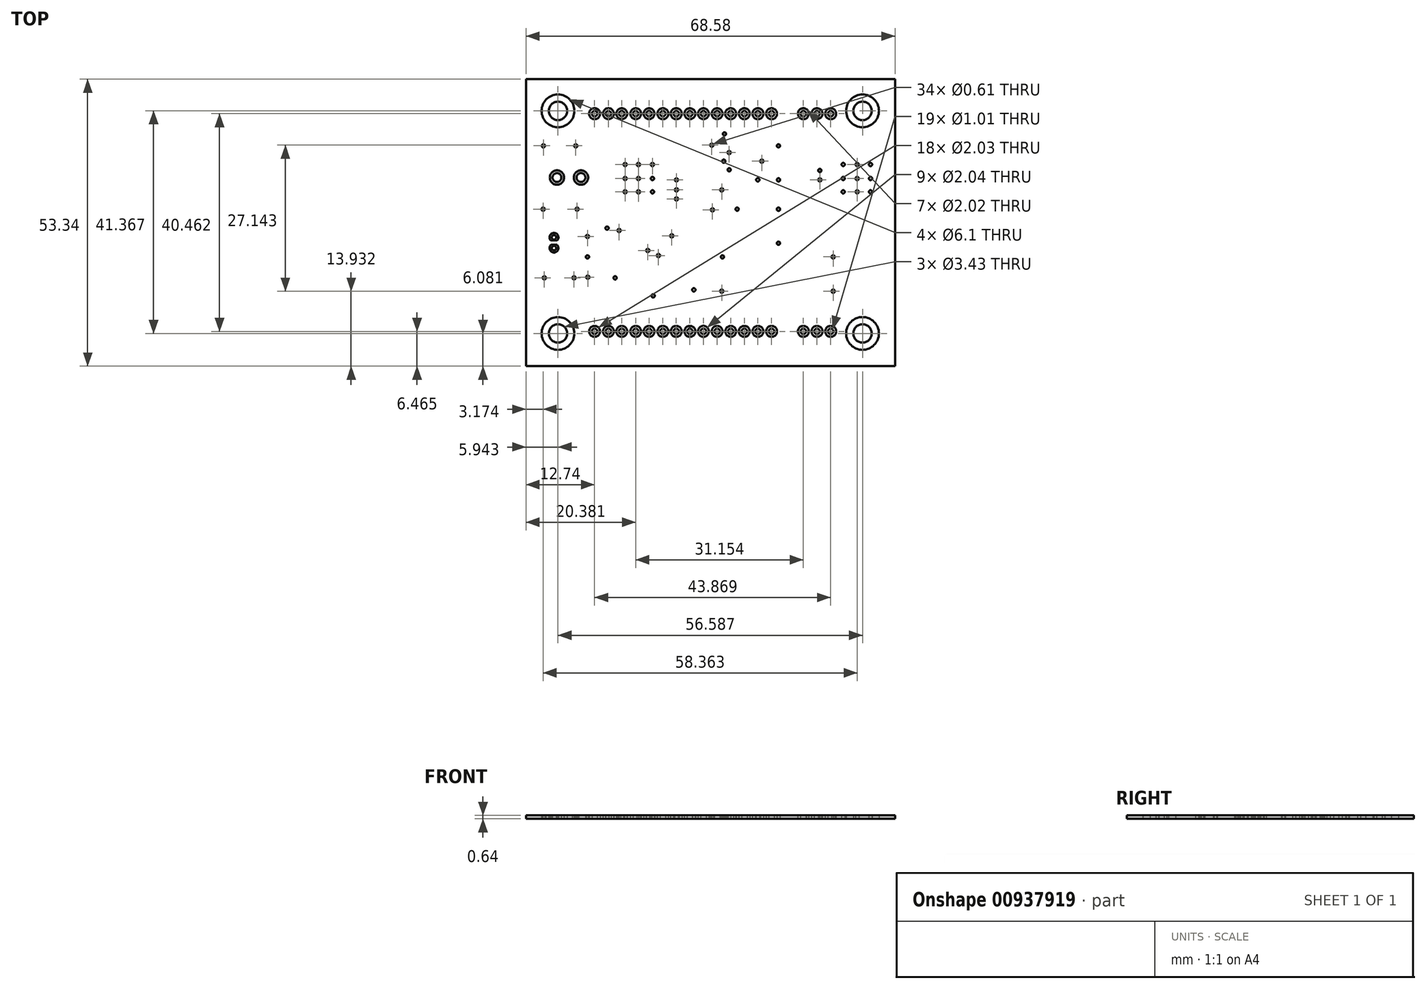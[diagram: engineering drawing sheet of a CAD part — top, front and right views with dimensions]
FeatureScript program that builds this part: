
annotation { "Feature Type Name" : "Feature", "Feature Type Description" : "" }
export const myFeature = defineFeature(function(context is Context, id is Id, definition is map)
    precondition{}
    {
        {
            var Q0;
            Q0=qCreatedBy(makeId("Top.planeOp"),FACE);
            var sketch = newSketch(context, id + "F0", { "sketchPlane" : qUnion([Q0])});
            skLineSegment(sketch, "E0.bottom", {"start": v(-43.28, 27.62) * mm, "end": v(25.3, 27.62) * mm});
            skLineSegment(sketch, "E0.top", {"start": v(-43.28, -25.72) * mm, "end": v(25.3, -25.72) * mm});
            skLineSegment(sketch, "E0.left", {"start": v(-43.28, 27.62) * mm, "end": v(-43.28, -25.72) * mm});
            skLineSegment(sketch, "E0.right", {"start": v(25.3, 27.62) * mm, "end": v(25.3, -25.72) * mm});
            skCircle(sketch, "E1", {"center": v(-37.34, -19.64) * mm, "radius": 1.71 * mm});
            skCircle(sketch, "E2", {"center": v(-37.34, -19.64) * mm, "radius": 3.05 * mm});
            skCircle(sketch, "E3", {"center": v(19.25, -19.64) * mm, "radius": 1.71 * mm});
            skCircle(sketch, "E4", {"center": v(19.25, -19.64) * mm, "radius": 3.05 * mm});
            skCircle(sketch, "E5", {"center": v(19.25, 21.73) * mm, "radius": 1.71 * mm});
            skCircle(sketch, "E6", {"center": v(19.25, 21.73) * mm, "radius": 3.05 * mm});
            skCircle(sketch, "E7", {"center": v(-37.34, 21.73) * mm, "radius": 1.71 * mm});
            skCircle(sketch, "E8", {"center": v(-37.34, 21.73) * mm, "radius": 3.05 * mm});
            skCircle(sketch, "E9", {"center": v(-38.09, -3.77) * mm, "radius": 0.4 * mm});
            skCircle(sketch, "E10", {"center": v(-38.09, -1.79) * mm, "radius": 0.4 * mm});
            skArc(sketch, "E11", {"start": v(-38.7, -2.35) * mm, "mid": v(-38.08, -0.95) * mm, "end": v(-37.48, -2.35) * mm});
            skLineSegment(sketch, "E12", {"start": v(-38.7, -2.35) * mm, "end": v(-37.48, -2.35) * mm});
            skArc(sketch, "E13", {"start": v(-37.51, -3.19) * mm, "mid": v(-38.09, -4.6) * mm, "end": v(-38.66, -3.19) * mm});
            skLineSegment(sketch, "E14", {"start": v(-38.66, -3.19) * mm, "end": v(-37.51, -3.19) * mm});
            skCircle(sketch, "E15", {"center": v(-37.53, 9.34) * mm, "radius": 0.82 * mm});
            skCircle(sketch, "E16", {"center": v(-37.53, 9.34) * mm, "radius": 1.33 * mm});
            skCircle(sketch, "E17", {"center": v(-33.07, 9.34) * mm, "radius": 0.83 * mm});
            skCircle(sketch, "E18", {"center": v(-33.07, 9.34) * mm, "radius": 1.33 * mm});
            skCircle(sketch, "E19", {"center": v(-30.54, -19.26) * mm, "radius": 0.5 * mm});
            skCircle(sketch, "E20", {"center": v(-30.54, -19.26) * mm, "radius": 1.02 * mm});
            skCircle(sketch, "E21", {"center": v(-27.96, -19.26) * mm, "radius": 0.5 * mm});
            skCircle(sketch, "E22", {"center": v(-25.49, -19.26) * mm, "radius": 0.5 * mm});
            skCircle(sketch, "E23", {"center": v(-22.9, -19.26) * mm, "radius": 0.5 * mm});
            skCircle(sketch, "E24", {"center": v(-20.42, -19.26) * mm, "radius": 0.5 * mm});
            skCircle(sketch, "E25", {"center": v(-17.85, -19.26) * mm, "radius": 0.5 * mm});
            skCircle(sketch, "E26", {"center": v(-15.36, -19.26) * mm, "radius": 0.5 * mm});
            skCircle(sketch, "E27", {"center": v(-12.83, -19.26) * mm, "radius": 0.51 * mm});
            skCircle(sketch, "E28", {"center": v(-10.31, -19.26) * mm, "radius": 0.5 * mm});
            skCircle(sketch, "E29", {"center": v(-7.76, -19.26) * mm, "radius": 0.5 * mm});
            skCircle(sketch, "E30", {"center": v(-5.25, -19.26) * mm, "radius": 0.5 * mm});
            skCircle(sketch, "E31", {"center": v(-2.71, -19.26) * mm, "radius": 0.5 * mm});
            skCircle(sketch, "E32", {"center": v(-0.19, -19.26) * mm, "radius": 0.5 * mm});
            skCircle(sketch, "E33", {"center": v(2.35, -19.26) * mm, "radius": 0.5 * mm});
            skCircle(sketch, "E34", {"center": v(-27.96, 21.2) * mm, "radius": 0.5 * mm});
            skCircle(sketch, "E35", {"center": v(-30.54, 21.2) * mm, "radius": 0.5 * mm});
            skCircle(sketch, "E36", {"center": v(-25.49, 21.2) * mm, "radius": 0.5 * mm});
            skCircle(sketch, "E37", {"center": v(-22.9, 21.2) * mm, "radius": 0.5 * mm});
            skCircle(sketch, "E38", {"center": v(-20.42, 21.2) * mm, "radius": 0.51 * mm});
            skCircle(sketch, "E39", {"center": v(-17.85, 21.2) * mm, "radius": 0.5 * mm});
            skCircle(sketch, "E40", {"center": v(-15.36, 21.2) * mm, "radius": 0.51 * mm});
            skCircle(sketch, "E41", {"center": v(-12.83, 21.2) * mm, "radius": 0.5 * mm});
            skCircle(sketch, "E42", {"center": v(-7.76, 21.2) * mm, "radius": 0.51 * mm});
            skCircle(sketch, "E43", {"center": v(-10.31, 21.2) * mm, "radius": 0.5 * mm});
            skCircle(sketch, "E44", {"center": v(-5.25, 21.2) * mm, "radius": 0.5 * mm});
            skCircle(sketch, "E45", {"center": v(-2.71, 21.2) * mm, "radius": 0.5 * mm});
            skCircle(sketch, "E46", {"center": v(-0.19, 21.2) * mm, "radius": 0.5 * mm});
            skCircle(sketch, "E47", {"center": v(2.35, 21.2) * mm, "radius": 0.5 * mm});
            skCircle(sketch, "E48", {"center": v(8.25, -19.26) * mm, "radius": 0.5 * mm});
            skCircle(sketch, "E49", {"center": v(10.79, -19.26) * mm, "radius": 0.5 * mm});
            skCircle(sketch, "E50", {"center": v(13.33, -19.26) * mm, "radius": 0.5 * mm});
            skCircle(sketch, "E51", {"center": v(8.25, 21.2) * mm, "radius": 0.51 * mm});
            skCircle(sketch, "E52", {"center": v(10.79, 21.2) * mm, "radius": 0.5 * mm});
            skCircle(sketch, "E53", {"center": v(13.33, 21.2) * mm, "radius": 0.51 * mm});
            skCircle(sketch, "E54", {"center": v(13.33, 21.2) * mm, "radius": 1.02 * mm});
            skCircle(sketch, "E55", {"center": v(10.79, 21.2) * mm, "radius": 1.02 * mm});
            skCircle(sketch, "E56", {"center": v(8.25, 21.2) * mm, "radius": 1.01 * mm});
            skCircle(sketch, "E57", {"center": v(2.35, 21.2) * mm, "radius": 1.02 * mm});
            skCircle(sketch, "E58", {"center": v(-0.19, 21.2) * mm, "radius": 1.02 * mm});
            skCircle(sketch, "E59", {"center": v(-2.71, 21.2) * mm, "radius": 1.01 * mm});
            skCircle(sketch, "E60", {"center": v(-5.25, 21.2) * mm, "radius": 1.02 * mm});
            skCircle(sketch, "E61", {"center": v(-7.76, 21.2) * mm, "radius": 1.01 * mm});
            skCircle(sketch, "E62", {"center": v(-10.31, 21.2) * mm, "radius": 1.01 * mm});
            skCircle(sketch, "E63", {"center": v(-12.83, 21.2) * mm, "radius": 1.01 * mm});
            skCircle(sketch, "E64", {"center": v(-15.36, 21.2) * mm, "radius": 1.02 * mm});
            skCircle(sketch, "E65", {"center": v(-17.85, 21.2) * mm, "radius": 1.02 * mm});
            skCircle(sketch, "E66", {"center": v(-20.42, 21.2) * mm, "radius": 1.01 * mm});
            skCircle(sketch, "E67", {"center": v(-22.9, 21.2) * mm, "radius": 1.01 * mm});
            skCircle(sketch, "E68", {"center": v(-25.49, 21.2) * mm, "radius": 1.01 * mm});
            skCircle(sketch, "E69", {"center": v(-27.96, 21.2) * mm, "radius": 1.02 * mm});
            skCircle(sketch, "E70", {"center": v(-30.54, 21.2) * mm, "radius": 1.02 * mm});
            skCircle(sketch, "E71", {"center": v(13.33, -19.26) * mm, "radius": 1.01 * mm});
            skCircle(sketch, "E72", {"center": v(10.79, -19.26) * mm, "radius": 1.02 * mm});
            skCircle(sketch, "E73", {"center": v(8.25, -19.26) * mm, "radius": 1.02 * mm});
            skCircle(sketch, "E74", {"center": v(2.35, -19.26) * mm, "radius": 1.02 * mm});
            skCircle(sketch, "E75", {"center": v(-0.19, -19.26) * mm, "radius": 1.02 * mm});
            skCircle(sketch, "E76", {"center": v(-2.71, -19.26) * mm, "radius": 1.01 * mm});
            skCircle(sketch, "E77", {"center": v(-5.25, -19.26) * mm, "radius": 1 * mm});
            skCircle(sketch, "E78", {"center": v(-7.76, -19.26) * mm, "radius": 1.01 * mm});
            skCircle(sketch, "E79", {"center": v(-10.31, -19.26) * mm, "radius": 1.02 * mm});
            skCircle(sketch, "E80", {"center": v(-12.83, -19.26) * mm, "radius": 1.02 * mm});
            skCircle(sketch, "E81", {"center": v(-15.36, -19.26) * mm, "radius": 1.02 * mm});
            skCircle(sketch, "E82", {"center": v(-17.85, -19.26) * mm, "radius": 1.01 * mm});
            skCircle(sketch, "E83", {"center": v(-20.42, -19.26) * mm, "radius": 1.01 * mm});
            skCircle(sketch, "E84", {"center": v(-22.9, -19.26) * mm, "radius": 1.01 * mm});
            skCircle(sketch, "E85", {"center": v(-25.49, -19.26) * mm, "radius": 1.01 * mm});
            skCircle(sketch, "E86", {"center": v(-27.96, -19.26) * mm, "radius": 1.02 * mm});
            skCircle(sketch, "E87", {"center": v(-39.87, -9.3) * mm, "radius": 0.3 * mm});
            skCircle(sketch, "E88", {"center": v(-34.36, -9.3) * mm, "radius": 0.3 * mm});
            skCircle(sketch, "E89", {"center": v(-31.8, -9.18) * mm, "radius": 0.3 * mm});
            skCircle(sketch, "E90", {"center": v(-26.73, -9.3) * mm, "radius": 0.3 * mm});
            skCircle(sketch, "E91", {"center": v(-31.86, -5.4) * mm, "radius": 0.31 * mm});
            skCircle(sketch, "E92", {"center": v(-31.86, -1.62) * mm, "radius": 0.3 * mm});
            skCircle(sketch, "E93", {"center": v(-28.21, -0.07) * mm, "radius": 0.3 * mm});
            skCircle(sketch, "E94", {"center": v(-33.79, 3.46) * mm, "radius": 0.3 * mm});
            skCircle(sketch, "E95", {"center": v(-40.1, 3.46) * mm, "radius": 0.3 * mm});
            skCircle(sketch, "E96", {"center": v(-40.05, 15.23) * mm, "radius": 0.3 * mm});
            skCircle(sketch, "E97", {"center": v(-34.03, 15.23) * mm, "radius": 0.3 * mm});
            skCircle(sketch, "E98", {"center": v(-24.86, 11.76) * mm, "radius": 0.3 * mm});
            skCircle(sketch, "E99", {"center": v(-22.4, 11.76) * mm, "radius": 0.3 * mm});
            skCircle(sketch, "E100", {"center": v(-22.39, 9.16) * mm, "radius": 0.3 * mm});
            skCircle(sketch, "E101", {"center": v(-24.86, 9.16) * mm, "radius": 0.3 * mm});
            skCircle(sketch, "E102", {"center": v(-19.79, 11.76) * mm, "radius": 0.3 * mm});
            skCircle(sketch, "E103", {"center": v(-19.79, 9.16) * mm, "radius": 0.3 * mm});
            skCircle(sketch, "E104", {"center": v(-19.78, 6.68) * mm, "radius": 0.3 * mm});
            skCircle(sketch, "E105", {"center": v(-22.39, 6.68) * mm, "radius": 0.3 * mm});
            skCircle(sketch, "E106", {"center": v(-24.86, 6.69) * mm, "radius": 0.3 * mm});
            skCircle(sketch, "E107", {"center": v(-15.33, 8.9) * mm, "radius": 0.3 * mm});
            skCircle(sketch, "E108", {"center": v(-15.32, 7.05) * mm, "radius": 0.3 * mm});
            skCircle(sketch, "E109", {"center": v(-15.32, 5.37) * mm, "radius": 0.3 * mm});
            skCircle(sketch, "E110", {"center": v(-25.98, -0.5) * mm, "radius": 0.3 * mm});
            skCircle(sketch, "E111", {"center": v(-20.65, -4.22) * mm, "radius": 0.3 * mm});
            skCircle(sketch, "E112", {"center": v(-18.67, -5.16) * mm, "radius": 0.3 * mm});
            skCircle(sketch, "E113", {"center": v(-16.2, -1.5) * mm, "radius": 0.3 * mm});
            skCircle(sketch, "E114", {"center": v(-6.78, -5.4) * mm, "radius": 0.3 * mm});
            skCircle(sketch, "E115", {"center": v(-19.66, -12.65) * mm, "radius": 0.3 * mm});
            skCircle(sketch, "E116", {"center": v(-12.1, -11.54) * mm, "radius": 0.3 * mm});
            skCircle(sketch, "E117", {"center": v(-6.9, -11.78) * mm, "radius": 0.3 * mm});
            skCircle(sketch, "E118", {"center": v(3.64, -2.86) * mm, "radius": 0.3 * mm});
            skCircle(sketch, "E119", {"center": v(13.8, -11.79) * mm, "radius": 0.3 * mm});
            skCircle(sketch, "E120", {"center": v(13.8, -5.4) * mm, "radius": 0.3 * mm});
            skCircle(sketch, "E121", {"center": v(-8.63, 3.33) * mm, "radius": 0.3 * mm});
            skCircle(sketch, "E122", {"center": v(-6.9, 7.05) * mm, "radius": 0.3 * mm});
            skCircle(sketch, "E123", {"center": v(-4.05, 3.46) * mm, "radius": 0.3 * mm});
            skCircle(sketch, "E124", {"center": v(3.63, 3.46) * mm, "radius": 0.31 * mm});
            skCircle(sketch, "E125", {"center": v(-0.2, 8.91) * mm, "radius": 0.3 * mm});
            skCircle(sketch, "E126", {"center": v(0.54, 12.38) * mm, "radius": 0.3 * mm});
            skCircle(sketch, "E127", {"center": v(-5.53, 10.78) * mm, "radius": 0.3 * mm});
            skCircle(sketch, "E128", {"center": v(-6.53, 12.38) * mm, "radius": 0.3 * mm});
            skCircle(sketch, "E129", {"center": v(-5.53, 13.98) * mm, "radius": 0.3 * mm});
            skCircle(sketch, "E130", {"center": v(-8.76, 15.36) * mm, "radius": 0.3 * mm});
            skCircle(sketch, "E131", {"center": v(-6.4, 17.46) * mm, "radius": 0.3 * mm});
            skCircle(sketch, "E132", {"center": v(3.63, 8.9) * mm, "radius": 0.3 * mm});
            skCircle(sketch, "E133", {"center": v(3.63, 15.24) * mm, "radius": 0.3 * mm});
            skCircle(sketch, "E134", {"center": v(11.32, 8.9) * mm, "radius": 0.3 * mm});
            skCircle(sketch, "E135", {"center": v(11.32, 10.64) * mm, "radius": 0.3 * mm});
            skCircle(sketch, "E136", {"center": v(15.65, 6.68) * mm, "radius": 0.3 * mm});
            skCircle(sketch, "E137", {"center": v(15.65, 9.16) * mm, "radius": 0.3 * mm});
            skCircle(sketch, "E138", {"center": v(15.66, 11.76) * mm, "radius": 0.3 * mm});
            skCircle(sketch, "E139", {"center": v(18.25, 11.76) * mm, "radius": 0.3 * mm});
            skCircle(sketch, "E140", {"center": v(18.25, 9.15) * mm, "radius": 0.3 * mm});
            skCircle(sketch, "E141", {"center": v(18.26, 6.68) * mm, "radius": 0.3 * mm});
            skCircle(sketch, "E142", {"center": v(20.73, 6.68) * mm, "radius": 0.3 * mm});
            skCircle(sketch, "E143", {"center": v(20.73, 9.16) * mm, "radius": 0.3 * mm});
            skCircle(sketch, "E144", {"center": v(20.73, 11.76) * mm, "radius": 0.3 * mm});
            skSolve(sketch);
        }
        {
            var Q0;
            Q0=makeQuery(id+"F0.imprint","IMPRINT",FACE,{"disambiguationData":[TD([[makeQuery(id+"F0.imprint","IMPRINT",EDGE,{"derivedFrom":sQuery(id+"F0.wireOp",EDGE,"E102")}),1.0]])]});
            var Q1;
            Q1=makeQuery(id+"F0.imprint","IMPRINT",FACE,{"disambiguationData":[TD([[makeQuery(id+"F0.imprint","IMPRINT",EDGE,{"derivedFrom":sQuery(id+"F0.wireOp",EDGE,"E1")}),-1.0]])]});
            var Q2;
            Q2=makeQuery(id+"F0.imprint","IMPRINT",FACE,{"disambiguationData":[TD([[makeQuery(id+"F0.imprint","IMPRINT",EDGE,{"derivedFrom":sQuery(id+"F0.wireOp",EDGE,"E3")}),-1.0]])]});
            var Q3;
            Q3=makeQuery(id+"F0.imprint","IMPRINT",FACE,{"disambiguationData":[TD([[makeQuery(id+"F0.imprint","IMPRINT",EDGE,{"derivedFrom":sQuery(id+"F0.wireOp",EDGE,"E5")}),-1.0]])]});
            var Q4;
            Q4=makeQuery(id+"F0.imprint","IMPRINT",FACE,{"disambiguationData":[TD([[makeQuery(id+"F0.imprint","IMPRINT",EDGE,{"derivedFrom":sQuery(id+"F0.wireOp",EDGE,"E7")}),-1.0]])]});
            var Q5;
            Q5=makeQuery(id+"F0.imprint","IMPRINT",FACE,{"disambiguationData":[TD([[makeQuery(id+"F0.imprint","IMPRINT",EDGE,{"derivedFrom":sQuery(id+"F0.wireOp",EDGE,"E23")}),-1.0]])]});
            var Q6;
            Q6=makeQuery(id+"F0.imprint","IMPRINT",FACE,{"disambiguationData":[TD([[makeQuery(id+"F0.imprint","IMPRINT",EDGE,{"derivedFrom":sQuery(id+"F0.wireOp",EDGE,"E39")}),-1.0]])]});
            var Q7;
            Q7=makeQuery(id+"F0.imprint","IMPRINT",FACE,{"disambiguationData":[TD([[makeQuery(id+"F0.imprint","IMPRINT",EDGE,{"derivedFrom":sQuery(id+"F0.wireOp",EDGE,"E21")}),-1.0]])]});
            var Q8;
            Q8=makeQuery(id+"F0.imprint","IMPRINT",FACE,{"disambiguationData":[TD([[makeQuery(id+"F0.imprint","IMPRINT",EDGE,{"derivedFrom":sQuery(id+"F0.wireOp",EDGE,"E37")}),-1.0]])]});
            var Q9;
            Q9=makeQuery(id+"F0.imprint","IMPRINT",FACE,{"disambiguationData":[TD([[makeQuery(id+"F0.imprint","IMPRINT",EDGE,{"derivedFrom":sQuery(id+"F0.wireOp",EDGE,"E53")}),-1.0]])]});
            var Q10;
            Q10=makeQuery(id+"F0.imprint","IMPRINT",FACE,{"disambiguationData":[TD([[makeQuery(id+"F0.imprint","IMPRINT",EDGE,{"derivedFrom":sQuery(id+"F0.wireOp",EDGE,"E25")}),-1.0]])]});
            var Q11;
            Q11=makeQuery(id+"F0.imprint","IMPRINT",FACE,{"disambiguationData":[TD([[makeQuery(id+"F0.imprint","IMPRINT",EDGE,{"derivedFrom":sQuery(id+"F0.wireOp",EDGE,"E41")}),-1.0]])]});
            var Q12;
            Q12=makeQuery(id+"F0.imprint","IMPRINT",FACE,{"disambiguationData":[TD([[makeQuery(id+"F0.imprint","IMPRINT",EDGE,{"derivedFrom":sQuery(id+"F0.wireOp",EDGE,"E27")}),-1.0]])]});
            var Q13;
            Q13=makeQuery(id+"F0.imprint","IMPRINT",FACE,{"disambiguationData":[TD([[makeQuery(id+"F0.imprint","IMPRINT",EDGE,{"derivedFrom":sQuery(id+"F0.wireOp",EDGE,"E44")}),-1.0]])]});
            var Q14;
            Q14=makeQuery(id+"F0.imprint","IMPRINT",FACE,{"disambiguationData":[TD([[makeQuery(id+"F0.imprint","IMPRINT",EDGE,{"derivedFrom":sQuery(id+"F0.wireOp",EDGE,"E30")}),-1.0]])]});
            var Q15;
            Q15=makeQuery(id+"F0.imprint","IMPRINT",FACE,{"disambiguationData":[TD([[makeQuery(id+"F0.imprint","IMPRINT",EDGE,{"derivedFrom":sQuery(id+"F0.wireOp",EDGE,"E46")}),-1.0]])]});
            var Q16;
            Q16=makeQuery(id+"F0.imprint","IMPRINT",FACE,{"disambiguationData":[TD([[makeQuery(id+"F0.imprint","IMPRINT",EDGE,{"derivedFrom":sQuery(id+"F0.wireOp",EDGE,"E32")}),-1.0]])]});
            var Q17;
            Q17=makeQuery(id+"F0.imprint","IMPRINT",FACE,{"disambiguationData":[TD([[makeQuery(id+"F0.imprint","IMPRINT",EDGE,{"derivedFrom":sQuery(id+"F0.wireOp",EDGE,"E48")}),-1.0]])]});
            var Q18;
            Q18=makeQuery(id+"F0.imprint","IMPRINT",FACE,{"disambiguationData":[TD([[makeQuery(id+"F0.imprint","IMPRINT",EDGE,{"derivedFrom":sQuery(id+"F0.wireOp",EDGE,"E15")}),-1.0]])]});
            var Q19;
            Q19=makeQuery(id+"F0.imprint","IMPRINT",FACE,{"disambiguationData":[TD([[makeQuery(id+"F0.imprint","IMPRINT",EDGE,{"derivedFrom":sQuery(id+"F0.wireOp",EDGE,"E34")}),-1.0]])]});
            var Q20;
            Q20=makeQuery(id+"F0.imprint","IMPRINT",FACE,{"disambiguationData":[TD([[makeQuery(id+"F0.imprint","IMPRINT",EDGE,{"derivedFrom":sQuery(id+"F0.wireOp",EDGE,"E17")}),-1.0]])]});
            var Q21;
            Q21=makeQuery(id+"F0.imprint","IMPRINT",FACE,{"disambiguationData":[TD([[makeQuery(id+"F0.imprint","IMPRINT",EDGE,{"derivedFrom":sQuery(id+"F0.wireOp",EDGE,"E35")}),-1.0]])]});
            var Q22;
            Q22=makeQuery(id+"F0.imprint","IMPRINT",FACE,{"disambiguationData":[TD([[makeQuery(id+"F0.imprint","IMPRINT",EDGE,{"derivedFrom":sQuery(id+"F0.wireOp",EDGE,"E51")}),-1.0]])]});
            var Q23;
            Q23=makeQuery(id+"F0.imprint","IMPRINT",FACE,{"disambiguationData":[TD([[makeQuery(id+"F0.imprint","IMPRINT",EDGE,{"derivedFrom":sQuery(id+"F0.wireOp",EDGE,"E19")}),-1.0]])]});
            var Q24;
            Q24=makeQuery(id+"F0.imprint","IMPRINT",FACE,{"disambiguationData":[TD([[makeQuery(id+"F0.imprint","IMPRINT",EDGE,{"derivedFrom":sQuery(id+"F0.wireOp",EDGE,"E92")}),1.0]])]});
            var Q25;
            Q25=makeQuery(id+"F0.imprint","IMPRINT",FACE,{"disambiguationData":[TD([[makeQuery(id+"F0.imprint","IMPRINT",EDGE,{"derivedFrom":sQuery(id+"F0.wireOp",EDGE,"E108")}),1.0]])]});
            var Q26;
            Q26=makeQuery(id+"F0.imprint","IMPRINT",FACE,{"disambiguationData":[TD([[makeQuery(id+"F0.imprint","IMPRINT",EDGE,{"derivedFrom":sQuery(id+"F0.wireOp",EDGE,"E124")}),1.0]])]});
            var Q27;
            Q27=makeQuery(id+"F0.imprint","IMPRINT",FACE,{"disambiguationData":[TD([[makeQuery(id+"F0.imprint","IMPRINT",EDGE,{"derivedFrom":sQuery(id+"F0.wireOp",EDGE,"E140")}),1.0]])]});
            var Q28;
            Q28=makeQuery(id+"F0.imprint","IMPRINT",FACE,{"disambiguationData":[TD([[makeQuery(id+"F0.imprint","IMPRINT",EDGE,{"derivedFrom":sQuery(id+"F0.wireOp",EDGE,"E90")}),1.0]])]});
            var Q29;
            Q29=makeQuery(id+"F0.imprint","IMPRINT",FACE,{"disambiguationData":[TD([[makeQuery(id+"F0.imprint","IMPRINT",EDGE,{"derivedFrom":sQuery(id+"F0.wireOp",EDGE,"E106")}),1.0]])]});
            var Q30;
            Q30=makeQuery(id+"F0.imprint","IMPRINT",FACE,{"disambiguationData":[TD([[makeQuery(id+"F0.imprint","IMPRINT",EDGE,{"derivedFrom":sQuery(id+"F0.wireOp",EDGE,"E122")}),1.0]])]});
            var Q31;
            Q31=makeQuery(id+"F0.imprint","IMPRINT",FACE,{"disambiguationData":[TD([[makeQuery(id+"F0.imprint","IMPRINT",EDGE,{"derivedFrom":sQuery(id+"F0.wireOp",EDGE,"E138")}),1.0]])]});
            var Q32;
            Q32=makeQuery(id+"F0.imprint","IMPRINT",FACE,{"disambiguationData":[TD([[makeQuery(id+"F0.imprint","IMPRINT",EDGE,{"derivedFrom":sQuery(id+"F0.wireOp",EDGE,"E91")}),1.0]])]});
            var Q33;
            Q33=makeQuery(id+"F0.imprint","IMPRINT",FACE,{"disambiguationData":[TD([[makeQuery(id+"F0.imprint","IMPRINT",EDGE,{"derivedFrom":sQuery(id+"F0.wireOp",EDGE,"E107")}),1.0]])]});
            var Q34;
            Q34=makeQuery(id+"F0.imprint","IMPRINT",FACE,{"disambiguationData":[TD([[makeQuery(id+"F0.imprint","IMPRINT",EDGE,{"derivedFrom":sQuery(id+"F0.wireOp",EDGE,"E123")}),1.0]])]});
            var Q35;
            Q35=makeQuery(id+"F0.imprint","IMPRINT",FACE,{"disambiguationData":[TD([[makeQuery(id+"F0.imprint","IMPRINT",EDGE,{"derivedFrom":sQuery(id+"F0.wireOp",EDGE,"E139")}),1.0]])]});
            var Q36;
            Q36=makeQuery(id+"F0.imprint","IMPRINT",FACE,{"disambiguationData":[TD([[makeQuery(id+"F0.imprint","IMPRINT",EDGE,{"derivedFrom":sQuery(id+"F0.wireOp",EDGE,"E93")}),1.0]])]});
            var Q37;
            Q37=makeQuery(id+"F0.imprint","IMPRINT",FACE,{"disambiguationData":[TD([[makeQuery(id+"F0.imprint","IMPRINT",EDGE,{"derivedFrom":sQuery(id+"F0.wireOp",EDGE,"E109")}),1.0]])]});
            var Q38;
            Q38=makeQuery(id+"F0.imprint","IMPRINT",FACE,{"disambiguationData":[TD([[makeQuery(id+"F0.imprint","IMPRINT",EDGE,{"derivedFrom":sQuery(id+"F0.wireOp",EDGE,"E125")}),1.0]])]});
            var Q39;
            Q39=makeQuery(id+"F0.imprint","IMPRINT",FACE,{"disambiguationData":[TD([[makeQuery(id+"F0.imprint","IMPRINT",EDGE,{"derivedFrom":sQuery(id+"F0.wireOp",EDGE,"E141")}),1.0]])]});
            var Q40;
            Q40=makeQuery(id+"F0.imprint","IMPRINT",FACE,{"disambiguationData":[TD([[makeQuery(id+"F0.imprint","IMPRINT",EDGE,{"derivedFrom":sQuery(id+"F0.wireOp",EDGE,"E94")}),1.0]])]});
            var Q41;
            Q41=makeQuery(id+"F0.imprint","IMPRINT",FACE,{"disambiguationData":[TD([[makeQuery(id+"F0.imprint","IMPRINT",EDGE,{"derivedFrom":sQuery(id+"F0.wireOp",EDGE,"E110")}),1.0]])]});
            var Q42;
            Q42=makeQuery(id+"F0.imprint","IMPRINT",FACE,{"disambiguationData":[TD([[makeQuery(id+"F0.imprint","IMPRINT",EDGE,{"derivedFrom":sQuery(id+"F0.wireOp",EDGE,"E126")}),1.0]])]});
            var Q43;
            Q43=makeQuery(id+"F0.imprint","IMPRINT",FACE,{"disambiguationData":[TD([[makeQuery(id+"F0.imprint","IMPRINT",EDGE,{"derivedFrom":sQuery(id+"F0.wireOp",EDGE,"E142")}),1.0]])]});
            var Q44;
            Q44=makeQuery(id+"F0.imprint","IMPRINT",FACE,{"disambiguationData":[TD([[makeQuery(id+"F0.imprint","IMPRINT",EDGE,{"derivedFrom":sQuery(id+"F0.wireOp",EDGE,"E95")}),1.0]])]});
            var Q45;
            Q45=makeQuery(id+"F0.imprint","IMPRINT",FACE,{"disambiguationData":[TD([[makeQuery(id+"F0.imprint","IMPRINT",EDGE,{"derivedFrom":sQuery(id+"F0.wireOp",EDGE,"E111")}),1.0]])]});
            var Q46;
            Q46=makeQuery(id+"F0.imprint","IMPRINT",FACE,{"disambiguationData":[TD([[makeQuery(id+"F0.imprint","IMPRINT",EDGE,{"derivedFrom":sQuery(id+"F0.wireOp",EDGE,"E127")}),1.0]])]});
            var Q47;
            Q47=makeQuery(id+"F0.imprint","IMPRINT",FACE,{"disambiguationData":[TD([[makeQuery(id+"F0.imprint","IMPRINT",EDGE,{"derivedFrom":sQuery(id+"F0.wireOp",EDGE,"E143")}),1.0]])]});
            var Q48;
            Q48=makeQuery(id+"F0.imprint","IMPRINT",FACE,{"disambiguationData":[TD([[makeQuery(id+"F0.imprint","IMPRINT",EDGE,{"derivedFrom":sQuery(id+"F0.wireOp",EDGE,"E42")}),-1.0]])]});
            var Q49;
            Q49=makeQuery(id+"F0.imprint","IMPRINT",FACE,{"disambiguationData":[TD([[makeQuery(id+"F0.imprint","IMPRINT",EDGE,{"derivedFrom":sQuery(id+"F0.wireOp",EDGE,"E96")}),1.0]])]});
            var Q50;
            Q50=makeQuery(id+"F0.imprint","IMPRINT",FACE,{"disambiguationData":[TD([[makeQuery(id+"F0.imprint","IMPRINT",EDGE,{"derivedFrom":sQuery(id+"F0.wireOp",EDGE,"E112")}),1.0]])]});
            var Q51;
            Q51=makeQuery(id+"F0.imprint","IMPRINT",FACE,{"disambiguationData":[TD([[makeQuery(id+"F0.imprint","IMPRINT",EDGE,{"derivedFrom":sQuery(id+"F0.wireOp",EDGE,"E128")}),1.0]])]});
            var Q52;
            Q52=makeQuery(id+"F0.imprint","IMPRINT",FACE,{"disambiguationData":[TD([[makeQuery(id+"F0.imprint","IMPRINT",EDGE,{"derivedFrom":sQuery(id+"F0.wireOp",EDGE,"E144")}),1.0]])]});
            var Q53;
            Q53=makeQuery(id+"F0.imprint","IMPRINT",FACE,{"disambiguationData":[TD([[makeQuery(id+"F0.imprint","IMPRINT",EDGE,{"derivedFrom":sQuery(id+"F0.wireOp",EDGE,"E43")}),-1.0]])]});
            var Q54;
            Q54=makeQuery(id+"F0.imprint","IMPRINT",FACE,{"disambiguationData":[TD([[makeQuery(id+"F0.imprint","IMPRINT",EDGE,{"derivedFrom":sQuery(id+"F0.wireOp",EDGE,"E97")}),1.0]])]});
            var Q55;
            Q55=makeQuery(id+"F0.imprint","IMPRINT",FACE,{"disambiguationData":[TD([[makeQuery(id+"F0.imprint","IMPRINT",EDGE,{"derivedFrom":sQuery(id+"F0.wireOp",EDGE,"E113")}),1.0]])]});
            var Q56;
            Q56=makeQuery(id+"F0.imprint","IMPRINT",FACE,{"disambiguationData":[TD([[makeQuery(id+"F0.imprint","IMPRINT",EDGE,{"derivedFrom":sQuery(id+"F0.wireOp",EDGE,"E129")}),1.0]])]});
            var Q57;
            Q57=makeQuery(id+"F0.imprint","IMPRINT",FACE,{"disambiguationData":[TD([[makeQuery(id+"F0.imprint","IMPRINT",EDGE,{"derivedFrom":sQuery(id+"F0.wireOp",EDGE,"E28")}),-1.0]])]});
            var Q58;
            Q58=makeQuery(id+"F0.imprint","IMPRINT",FACE,{"disambiguationData":[TD([[makeQuery(id+"F0.imprint","IMPRINT",EDGE,{"derivedFrom":sQuery(id+"F0.wireOp",EDGE,"E98")}),1.0]])]});
            var Q59;
            Q59=makeQuery(id+"F0.imprint","IMPRINT",FACE,{"disambiguationData":[TD([[makeQuery(id+"F0.imprint","IMPRINT",EDGE,{"derivedFrom":sQuery(id+"F0.wireOp",EDGE,"E114")}),1.0]])]});
            var Q60;
            Q60=makeQuery(id+"F0.imprint","IMPRINT",FACE,{"disambiguationData":[TD([[makeQuery(id+"F0.imprint","IMPRINT",EDGE,{"derivedFrom":sQuery(id+"F0.wireOp",EDGE,"E130")}),1.0]])]});
            var Q61;
            Q61=makeQuery(id+"F0.imprint","IMPRINT",FACE,{"disambiguationData":[TD([[makeQuery(id+"F0.imprint","IMPRINT",EDGE,{"derivedFrom":sQuery(id+"F0.wireOp",EDGE,"E99")}),1.0]])]});
            var Q62;
            Q62=makeQuery(id+"F0.imprint","IMPRINT",FACE,{"disambiguationData":[TD([[makeQuery(id+"F0.imprint","IMPRINT",EDGE,{"derivedFrom":sQuery(id+"F0.wireOp",EDGE,"E115")}),1.0]])]});
            var Q63;
            Q63=makeQuery(id+"F0.imprint","IMPRINT",FACE,{"disambiguationData":[TD([[makeQuery(id+"F0.imprint","IMPRINT",EDGE,{"derivedFrom":sQuery(id+"F0.wireOp",EDGE,"E131")}),1.0]])]});
            var Q64;
            Q64=makeQuery(id+"F0.imprint","IMPRINT",FACE,{"disambiguationData":[TD([[makeQuery(id+"F0.imprint","IMPRINT",EDGE,{"derivedFrom":sQuery(id+"F0.wireOp",EDGE,"E100")}),1.0]])]});
            var Q65;
            Q65=makeQuery(id+"F0.imprint","IMPRINT",FACE,{"disambiguationData":[TD([[makeQuery(id+"F0.imprint","IMPRINT",EDGE,{"derivedFrom":sQuery(id+"F0.wireOp",EDGE,"E116")}),1.0]])]});
            var Q66;
            Q66=makeQuery(id+"F0.imprint","IMPRINT",FACE,{"disambiguationData":[TD([[makeQuery(id+"F0.imprint","IMPRINT",EDGE,{"derivedFrom":sQuery(id+"F0.wireOp",EDGE,"E132")}),1.0]])]});
            var Q67;
            Q67=makeQuery(id+"F0.imprint","IMPRINT",FACE,{"disambiguationData":[TD([[makeQuery(id+"F0.imprint","IMPRINT",EDGE,{"derivedFrom":sQuery(id+"F0.wireOp",EDGE,"E101")}),1.0]])]});
            var Q68;
            Q68=makeQuery(id+"F0.imprint","IMPRINT",FACE,{"disambiguationData":[TD([[makeQuery(id+"F0.imprint","IMPRINT",EDGE,{"derivedFrom":sQuery(id+"F0.wireOp",EDGE,"E117")}),1.0]])]});
            var Q69;
            Q69=makeQuery(id+"F0.imprint","IMPRINT",FACE,{"disambiguationData":[TD([[makeQuery(id+"F0.imprint","IMPRINT",EDGE,{"derivedFrom":sQuery(id+"F0.wireOp",EDGE,"E133")}),1.0]])]});
            var Q70;
            Q70=makeQuery(id+"F0.imprint","IMPRINT",FACE,{"disambiguationData":[TD([[makeQuery(id+"F0.imprint","IMPRINT",EDGE,{"derivedFrom":sQuery(id+"F0.wireOp",EDGE,"E118")}),1.0]])]});
            var Q71;
            Q71=makeQuery(id+"F0.imprint","IMPRINT",FACE,{"disambiguationData":[TD([[makeQuery(id+"F0.imprint","IMPRINT",EDGE,{"derivedFrom":sQuery(id+"F0.wireOp",EDGE,"E134")}),1.0]])]});
            var Q72;
            Q72=makeQuery(id+"F0.imprint","IMPRINT",FACE,{"disambiguationData":[TD([[makeQuery(id+"F0.imprint","IMPRINT",EDGE,{"derivedFrom":sQuery(id+"F0.wireOp",EDGE,"E49")}),-1.0]])]});
            var Q73;
            Q73=makeQuery(id+"F0.imprint","IMPRINT",FACE,{"disambiguationData":[TD([[makeQuery(id+"F0.imprint","IMPRINT",EDGE,{"derivedFrom":sQuery(id+"F0.wireOp",EDGE,"E87")}),1.0]])]});
            var Q74;
            Q74=makeQuery(id+"F0.imprint","IMPRINT",FACE,{"disambiguationData":[TD([[makeQuery(id+"F0.imprint","IMPRINT",EDGE,{"derivedFrom":sQuery(id+"F0.wireOp",EDGE,"E103")}),1.0]])]});
            var Q75;
            Q75=makeQuery(id+"F0.imprint","IMPRINT",FACE,{"disambiguationData":[TD([[makeQuery(id+"F0.imprint","IMPRINT",EDGE,{"derivedFrom":sQuery(id+"F0.wireOp",EDGE,"E119")}),1.0]])]});
            var Q76;
            Q76=makeQuery(id+"F0.imprint","IMPRINT",FACE,{"disambiguationData":[TD([[makeQuery(id+"F0.imprint","IMPRINT",EDGE,{"derivedFrom":sQuery(id+"F0.wireOp",EDGE,"E135")}),1.0]])]});
            var Q77;
            Q77=makeQuery(id+"F0.imprint","IMPRINT",FACE,{"disambiguationData":[TD([[makeQuery(id+"F0.imprint","IMPRINT",EDGE,{"derivedFrom":sQuery(id+"F0.wireOp",EDGE,"E50")}),-1.0]])]});
            var Q78;
            Q78=makeQuery(id+"F0.imprint","IMPRINT",FACE,{"disambiguationData":[TD([[makeQuery(id+"F0.imprint","IMPRINT",EDGE,{"derivedFrom":sQuery(id+"F0.wireOp",EDGE,"E88")}),1.0]])]});
            var Q79;
            Q79=makeQuery(id+"F0.imprint","IMPRINT",FACE,{"disambiguationData":[TD([[makeQuery(id+"F0.imprint","IMPRINT",EDGE,{"derivedFrom":sQuery(id+"F0.wireOp",EDGE,"E104")}),1.0]])]});
            var Q80;
            Q80=makeQuery(id+"F0.imprint","IMPRINT",FACE,{"disambiguationData":[TD([[makeQuery(id+"F0.imprint","IMPRINT",EDGE,{"derivedFrom":sQuery(id+"F0.wireOp",EDGE,"E120")}),1.0]])]});
            var Q81;
            Q81=makeQuery(id+"F0.imprint","IMPRINT",FACE,{"disambiguationData":[TD([[makeQuery(id+"F0.imprint","IMPRINT",EDGE,{"derivedFrom":sQuery(id+"F0.wireOp",EDGE,"E136")}),1.0]])]});
            var Q82;
            Q82=makeQuery(id+"F0.imprint","IMPRINT",FACE,{"disambiguationData":[TD([[makeQuery(id+"F0.imprint","IMPRINT",EDGE,{"derivedFrom":sQuery(id+"F0.wireOp",EDGE,"E89")}),1.0]])]});
            var Q83;
            Q83=makeQuery(id+"F0.imprint","IMPRINT",FACE,{"disambiguationData":[TD([[makeQuery(id+"F0.imprint","IMPRINT",EDGE,{"derivedFrom":sQuery(id+"F0.wireOp",EDGE,"E105")}),1.0]])]});
            var Q84;
            Q84=makeQuery(id+"F0.imprint","IMPRINT",FACE,{"disambiguationData":[TD([[makeQuery(id+"F0.imprint","IMPRINT",EDGE,{"derivedFrom":sQuery(id+"F0.wireOp",EDGE,"E121")}),1.0]])]});
            var Q85;
            Q85=makeQuery(id+"F0.imprint","IMPRINT",FACE,{"disambiguationData":[TD([[makeQuery(id+"F0.imprint","IMPRINT",EDGE,{"derivedFrom":sQuery(id+"F0.wireOp",EDGE,"E137")}),1.0]])]});
            var Q86;
            Q86=makeQuery(id+"F0.imprint","IMPRINT",FACE,{"disambiguationData":[TD([[makeQuery(id+"F0.imprint","IMPRINT",EDGE,{"derivedFrom":sQuery(id+"F0.wireOp",EDGE,"E52")}),-1.0]])]});
            var Q87;
            Q87=makeQuery(id+"F0.imprint","IMPRINT",FACE,{"disambiguationData":[TD([[makeQuery(id+"F0.imprint","IMPRINT",EDGE,{"derivedFrom":sQuery(id+"F0.wireOp",EDGE,"E22")}),-1.0]])]});
            var Q88;
            Q88=makeQuery(id+"F0.imprint","IMPRINT",FACE,{"disambiguationData":[TD([[makeQuery(id+"F0.imprint","IMPRINT",EDGE,{"derivedFrom":sQuery(id+"F0.wireOp",EDGE,"E38")}),-1.0]])]});
            var Q89;
            Q89=makeQuery(id+"F0.imprint","IMPRINT",FACE,{"disambiguationData":[TD([[makeQuery(id+"F0.imprint","IMPRINT",EDGE,{"derivedFrom":sQuery(id+"F0.wireOp",EDGE,"E24")}),-1.0]])]});
            var Q90;
            Q90=makeQuery(id+"F0.imprint","IMPRINT",FACE,{"disambiguationData":[TD([[makeQuery(id+"F0.imprint","IMPRINT",EDGE,{"derivedFrom":sQuery(id+"F0.wireOp",EDGE,"E40")}),-1.0]])]});
            var Q91;
            Q91=makeQuery(id+"F0.imprint","IMPRINT",FACE,{"disambiguationData":[TD([[makeQuery(id+"F0.imprint","IMPRINT",EDGE,{"derivedFrom":sQuery(id+"F0.wireOp",EDGE,"E26")}),-1.0]])]});
            var Q92;
            Q92=makeQuery(id+"F0.imprint","IMPRINT",FACE,{"disambiguationData":[TD([[makeQuery(id+"F0.imprint","IMPRINT",EDGE,{"derivedFrom":sQuery(id+"F0.wireOp",EDGE,"E45")}),-1.0]])]});
            var Q93;
            Q93=makeQuery(id+"F0.imprint","IMPRINT",FACE,{"disambiguationData":[TD([[makeQuery(id+"F0.imprint","IMPRINT",EDGE,{"derivedFrom":sQuery(id+"F0.wireOp",EDGE,"E31")}),-1.0]])]});
            var Q94;
            Q94=makeQuery(id+"F0.imprint","IMPRINT",FACE,{"disambiguationData":[TD([[makeQuery(id+"F0.imprint","IMPRINT",EDGE,{"derivedFrom":sQuery(id+"F0.wireOp",EDGE,"E47")}),-1.0]])]});
            var Q95;
            Q95=makeQuery(id+"F0.imprint","IMPRINT",FACE,{"disambiguationData":[TD([[makeQuery(id+"F0.imprint","IMPRINT",EDGE,{"derivedFrom":sQuery(id+"F0.wireOp",EDGE,"E9")}),-1.0]])]});
            var Q96;
            Q96=makeQuery(id+"F0.imprint","IMPRINT",FACE,{"disambiguationData":[TD([[makeQuery(id+"F0.imprint","IMPRINT",EDGE,{"derivedFrom":sQuery(id+"F0.wireOp",EDGE,"E10")}),-1.0]])]});
            var Q97;
            Q97=makeQuery(id+"F0.imprint","IMPRINT",FACE,{"disambiguationData":[TD([[makeQuery(id+"F0.imprint","IMPRINT",EDGE,{"derivedFrom":sQuery(id+"F0.wireOp",EDGE,"E33")}),-1.0]])]});
            var Q98;
            Q98=makeQuery(id+"F0.imprint","IMPRINT",FACE,{"disambiguationData":[TD([[makeQuery(id+"F0.imprint","IMPRINT",EDGE,{"derivedFrom":sQuery(id+"F0.wireOp",EDGE,"E36")}),-1.0]])]});
            var Q99;
            Q99=makeQuery(id+"F0.imprint","IMPRINT",FACE,{"disambiguationData":[TD([[makeQuery(id+"F0.imprint","IMPRINT",EDGE,{"derivedFrom":sQuery(id+"F0.wireOp",EDGE,"E29")}),-1.0]])]});
            extrude(context, id + "F1", {"entities" : qUnion([Q0, Q1, Q2, Q3, Q4, Q5, Q6, Q7, Q8, Q9, Q10, Q11, Q12, Q13, Q14, Q15, Q16, Q17, Q18, Q19, Q20, Q21, Q22, Q23, Q24, Q25, Q26, Q27, Q28, Q29, Q30, Q31, Q32, Q33, Q34, Q35, Q36, Q37, Q38, Q39, Q40, Q41, Q42, Q43, Q44, Q45, Q46, Q47, Q48, Q49, Q50, Q51, Q52, Q53, Q54, Q55, Q56, Q57, Q58, Q59, Q60, Q61, Q62, Q63, Q64, Q65, Q66, Q67, Q68, Q69, Q70, Q71, Q72, Q73, Q74, Q75, Q76, Q77, Q78, Q79, Q80, Q81, Q82, Q83, Q84, Q85, Q86, Q87, Q88, Q89, Q90, Q91, Q92, Q93, Q94, Q95, Q96, Q97, Q98, Q99]), "depth" : 0.64 * mm, "offsetDistance" : 25.4 * mm});
        }
        {
            var Q0;
            Q0 = qSketchRegion(id + "F0", true);
            extrude(context, id + "F2", {"entities" : qUnion([Q0]), "depth" : 0.64 * mm, "offsetDistance" : 25.4 * mm});
        }
    });
